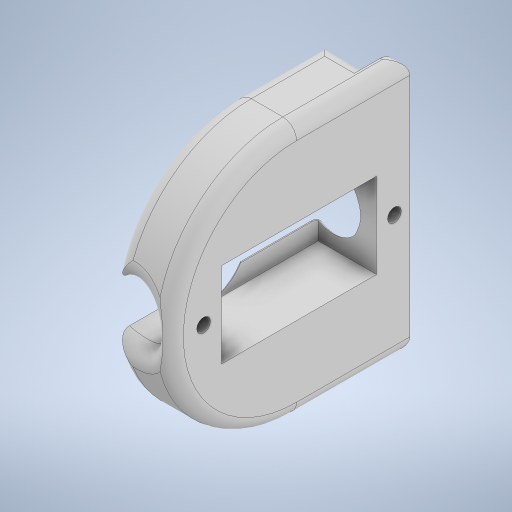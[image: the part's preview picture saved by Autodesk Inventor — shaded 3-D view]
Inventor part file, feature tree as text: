
AUTODESK INVENTOR PART (.ipt)
format: ipt  version: 2023.2 (Build 272271000, 271)  size: 422,912 bytes
history: native  units: mm
features: sketch x9, extrude x6, hole x3, fillet x2
ambient origin geometry x8: Origin, YZ Plane, XZ Plane, XY Plane, X Axis, Y Axis, Z Axis, Center Point
bodies: Solid1 (feature_tree)
feature tree (20):
  extrude  "Extrusion1"  Depth=12.6mm
  extrude  "Extrusion2"  Depth=8.0mm
  hole  "Hole1"  [1 undecoded]
  hole  "Hole2"  [1 undecoded]
  fillet  "Fillet1"  Radius=27.8mm
  hole  "Hole3"  [1 undecoded]
  extrude  "Extrusion3"  Depth=8.5mm TaperAngle=0.0deg
  extrude  "Extrusion4"  Depth=10.0mm TaperAngle=0.0deg
  extrude  "Extrusion5"  Depth=2.0mm TaperAngle=0.0deg
  extrude  "Extrusion6"  Depth=2.0mm
  fillet  "Fillet2"  [1 undecoded]
  sketch  "Sketch3"  dims[d0=37.0mm d1=12.6mm]
  sketch  "Sketch4"  dims[d2=35.0mm d3=0.0mm d4=8.0mm]
  sketch  "Sketch5"  dims[d5=3.8mm d6=0.0mm d7=24.1mm]
  sketch  "Sketch6"  dims[d8=2.0mm d9=6.0mm d10=4.0mm d11=2.0mm d12=90.0deg d13=8.0mm d14=0.0mm]
  sketch  "Sketch8"  dims[d15=8.0mm d16=6.0mm d17=4.0mm d18=2.0mm d19=90.0deg d20=8.0mm d21=0.0mm d22=2.0mm d25=27.8mm]
  sketch  "Sketch9"  dims[d26=4.502mm]
  sketch  "Sketch10"  dims[d27=2.0mm d28=6.0mm d29=4.0mm d30=2.0mm d31=90.0deg d32=8.0mm d33=0.0mm d34=12.4mm]
  sketch  "Sketch11"  dims[d35=22.6mm d36=8.5mm d37=0.0mm]
  sketch  "Sketch12"  dims[d38=6.1mm d39=10.0mm d40=0.0mm d41=35.0mm d42=0.0mm d43=4.0mm d44=0.0mm d45=0.0mm d46=2.0mm d47=0.0mm d48=0.0mm d49=0.0mm]
note: 4 required parameter values undecoded (feature->parameter linkage not recoverable at this tier; creation-order binding heuristic only, values carry confidence <= 0.55)
